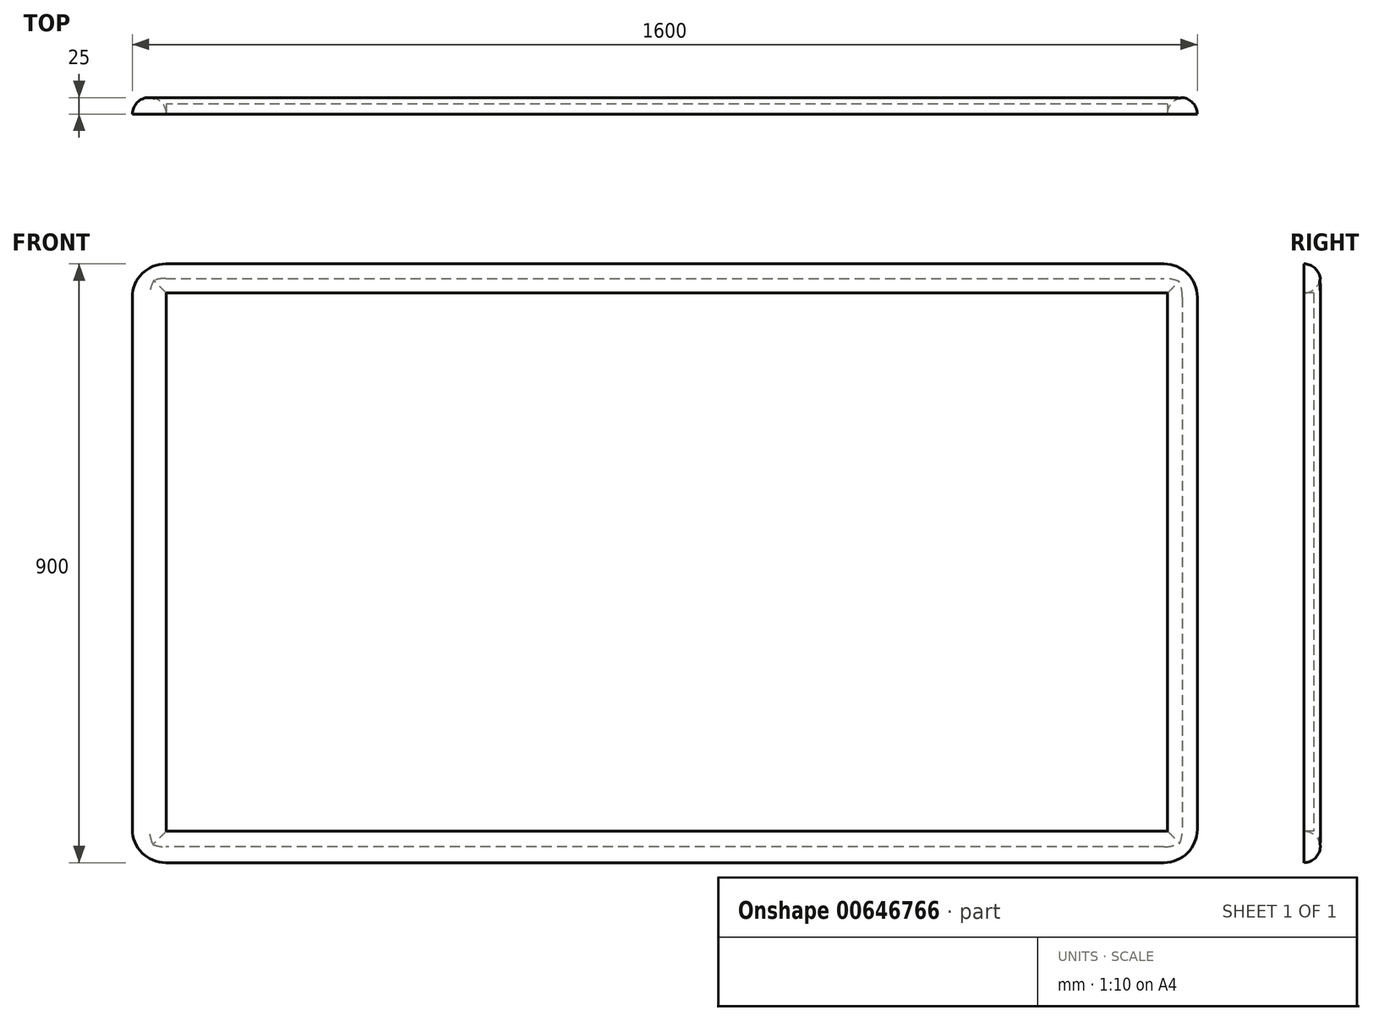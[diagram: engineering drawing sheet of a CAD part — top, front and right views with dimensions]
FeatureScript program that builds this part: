
annotation { "Feature Type Name" : "Feature", "Feature Type Description" : "" }
export const myFeature = defineFeature(function(context is Context, id is Id, definition is map)
    precondition{}
    {
        {
            var Q0;
            Q0=qCreatedBy(makeId("Front.planeOp"),FACE);
            var sketch = newSketch(context, id + "F0", { "sketchPlane" : qUnion([Q0])});
            skLineSegment(sketch, "E0.bottom", {"start": v(801.75, 391.43) * mm, "end": v(-798.25, 391.43) * mm});
            skLineSegment(sketch, "E0.top", {"start": v(801.75, -508.57) * mm, "end": v(-798.25, -508.57) * mm});
            skLineSegment(sketch, "E0.left", {"start": v(801.75, 391.43) * mm, "end": v(801.75, -508.57) * mm});
            skLineSegment(sketch, "E0.right", {"start": v(-798.25, 391.43) * mm, "end": v(-798.25, -508.57) * mm});
            skLineSegment(sketch, "E1.bottom", {"start": v(757.12, 347.64) * mm, "end": v(-747.15, 347.64) * mm});
            skLineSegment(sketch, "E1.top", {"start": v(757.12, -461.1) * mm, "end": v(-747.15, -461.1) * mm});
            skLineSegment(sketch, "E1.left", {"start": v(757.12, 347.64) * mm, "end": v(757.12, -461.1) * mm});
            skLineSegment(sketch, "E1.right", {"start": v(-747.15, 347.64) * mm, "end": v(-747.15, -461.1) * mm});
            skSolve(sketch);
        }
        {
            var Q0;
            Q0=makeQuery(id+"F0.imprint","IMPRINT",FACE,{"disambiguationData":[TD([[makeQuery(id+"F0.imprint","IMPRINT",EDGE,{"derivedFrom":sQuery(id+"F0.wireOp",EDGE,"E0.bottom")}),1.0]])]});
            extrude(context, id + "F1", {"entities" : qUnion([Q0]), "depth" : 25 * mm, "offsetDistance" : 25 * mm});
        }
        {
            var Q0;
            Q0=makeQuery(id+"F1.opExtrude","CAP_FACE",FACE,{"disambiguationData":[OSD([sQuery(id+"F0.wireOp",EDGE,"E0.bottom"),sQuery(id+"F0.wireOp",EDGE,"E0.top"),sQuery(id+"F0.wireOp",EDGE,"E0.left"),sQuery(id+"F0.wireOp",EDGE,"E0.right"),sQuery(id+"F0.wireOp",EDGE,"E1.bottom"),sQuery(id+"F0.wireOp",EDGE,"E1.top"),sQuery(id+"F0.wireOp",EDGE,"E1.left"),sQuery(id+"F0.wireOp",EDGE,"E1.right")])],"isStart":false});
            var sketch = newSketch(context, id + "F2", { "sketchPlane" : qUnion([Q0])});
            skLineSegment(sketch, "E2.bottom", {"start": v(757.12, 347.64) * mm, "end": v(-747.15, 347.64) * mm});
            skLineSegment(sketch, "E2.top", {"start": v(757.12, -461.1) * mm, "end": v(-747.15, -461.1) * mm});
            skLineSegment(sketch, "E2.left", {"start": v(757.12, 347.64) * mm, "end": v(757.12, -461.1) * mm});
            skLineSegment(sketch, "E2.right", {"start": v(-747.15, 347.64) * mm, "end": v(-747.15, -461.1) * mm});
            skSolve(sketch);
        }
        {
            var Q0;
            Q0 = qSketchRegion(id + "F2", true);
            extrude(context, id + "F3", {"entities" : qUnion([Q0]), "oppositeDirection" : true, "depth" : 15 * mm, "offsetDistance" : 25 * mm});
        }
        {
            var Q0;
            Q0=makeQuery(id+"F1.opExtrude","SWEPT_EDGE",EDGE,{"disambiguationData":[OSD([sQuery(id+"F0.wireOp",EDGE,"E0.bottom"),sQuery(id+"F0.wireOp",EDGE,"E0.left")])]});
            var Q1;
            Q1=makeQuery(id+"F1.opExtrude","SWEPT_EDGE",EDGE,{"disambiguationData":[OSD([sQuery(id+"F0.wireOp",EDGE,"E0.top"),sQuery(id+"F0.wireOp",EDGE,"E0.left")])]});
            var Q2;
            Q2=makeQuery(id+"F1.opExtrude","SWEPT_EDGE",EDGE,{"disambiguationData":[OSD([sQuery(id+"F0.wireOp",EDGE,"E0.top"),sQuery(id+"F0.wireOp",EDGE,"E0.right")])]});
            var Q3;
            Q3=makeQuery(id+"F1.opExtrude","SWEPT_EDGE",EDGE,{"disambiguationData":[OSD([sQuery(id+"F0.wireOp",EDGE,"E0.bottom"),sQuery(id+"F0.wireOp",EDGE,"E0.right")])]});
            fillet(context, id + "F4", {"entities" : qUnion([Q0, Q1, Q2, Q3]), "radius" : 50 * mm, "tangentPropagation" : true, "allowEdgeOverflow" : false});
        }
        {
            var Q0;
            Q0=makeQuery(id+"F1.opExtrude","CAP_EDGE",EDGE,{"disambiguationData":[OSD([sQuery(id+"F0.wireOp",EDGE,"E1.left")])],"isStart":true});
            var Q1;
            Q1=makeQuery(id+"F1.opExtrude","CAP_EDGE",EDGE,{"disambiguationData":[OSD([sQuery(id+"F0.wireOp",EDGE,"E1.bottom")])],"isStart":true});
            var Q2;
            Q2=makeQuery(id+"F1.opExtrude","CAP_EDGE",EDGE,{"disambiguationData":[OSD([sQuery(id+"F0.wireOp",EDGE,"E1.top")])],"isStart":true});
            var Q3;
            Q3=makeQuery(id+"F1.opExtrude","CAP_EDGE",EDGE,{"disambiguationData":[OSD([sQuery(id+"F0.wireOp",EDGE,"E1.right")])],"isStart":true});
            var Q4;
            Q4=makeQuery(id+"F1.opExtrude","CAP_EDGE",EDGE,{"disambiguationData":[OSD([sQuery(id+"F0.wireOp",EDGE,"E0.right")])],"isStart":true});
            var Q5;
            {var subQ0=sQuery(id+"F0.wireOp",EDGE,"E0.right");var subQ1=sQuery(id+"F0.wireOp",EDGE,"E0.bottom");Q5=makeQuery(id+"F4.opFillet","BLEND_EDGE",EDGE,{"blendedFrom":[makeQuery(id+"F1.opExtrude","SWEPT_EDGE",EDGE,{"disambiguationData":[OSD([subQ1,subQ0])]}),makeQuery(id+"F1.opExtrude","CAP_FACE",FACE,{"disambiguationData":[OSD([subQ1,sQuery(id+"F0.wireOp",EDGE,"E0.top"),sQuery(id+"F0.wireOp",EDGE,"E0.left"),subQ0,sQuery(id+"F0.wireOp",EDGE,"E1.bottom"),sQuery(id+"F0.wireOp",EDGE,"E1.top"),sQuery(id+"F0.wireOp",EDGE,"E1.left"),sQuery(id+"F0.wireOp",EDGE,"E1.right")])],"isStart":true})],"blendedInto":[makeQuery(id+"F1.opExtrude","CAP_FACE",FACE,{"disambiguationData":[OSD([subQ1,sQuery(id+"F0.wireOp",EDGE,"E0.top"),sQuery(id+"F0.wireOp",EDGE,"E0.left"),subQ0,sQuery(id+"F0.wireOp",EDGE,"E1.bottom"),sQuery(id+"F0.wireOp",EDGE,"E1.top"),sQuery(id+"F0.wireOp",EDGE,"E1.left"),sQuery(id+"F0.wireOp",EDGE,"E1.right")])],"isStart":true})]});}
            var Q6;
            Q6=makeQuery(id+"F1.opExtrude","CAP_EDGE",EDGE,{"disambiguationData":[OSD([sQuery(id+"F0.wireOp",EDGE,"E0.bottom")])],"isStart":true});
            var Q7;
            {var subQ0=sQuery(id+"F0.wireOp",EDGE,"E0.left");var subQ1=sQuery(id+"F0.wireOp",EDGE,"E0.bottom");Q7=makeQuery(id+"F4.opFillet","BLEND_EDGE",EDGE,{"blendedFrom":[makeQuery(id+"F1.opExtrude","SWEPT_EDGE",EDGE,{"disambiguationData":[OSD([subQ1,subQ0])]}),makeQuery(id+"F1.opExtrude","CAP_FACE",FACE,{"disambiguationData":[OSD([subQ1,sQuery(id+"F0.wireOp",EDGE,"E0.top"),subQ0,sQuery(id+"F0.wireOp",EDGE,"E0.right"),sQuery(id+"F0.wireOp",EDGE,"E1.bottom"),sQuery(id+"F0.wireOp",EDGE,"E1.top"),sQuery(id+"F0.wireOp",EDGE,"E1.left"),sQuery(id+"F0.wireOp",EDGE,"E1.right")])],"isStart":true})],"blendedInto":[makeQuery(id+"F1.opExtrude","CAP_FACE",FACE,{"disambiguationData":[OSD([subQ1,sQuery(id+"F0.wireOp",EDGE,"E0.top"),subQ0,sQuery(id+"F0.wireOp",EDGE,"E0.right"),sQuery(id+"F0.wireOp",EDGE,"E1.bottom"),sQuery(id+"F0.wireOp",EDGE,"E1.top"),sQuery(id+"F0.wireOp",EDGE,"E1.left"),sQuery(id+"F0.wireOp",EDGE,"E1.right")])],"isStart":true})]});}
            var Q8;
            Q8=makeQuery(id+"F1.opExtrude","CAP_EDGE",EDGE,{"disambiguationData":[OSD([sQuery(id+"F0.wireOp",EDGE,"E0.left")])],"isStart":true});
            var Q9;
            {var subQ0=sQuery(id+"F0.wireOp",EDGE,"E0.left");var subQ1=sQuery(id+"F0.wireOp",EDGE,"E0.top");Q9=makeQuery(id+"F4.opFillet","BLEND_EDGE",EDGE,{"blendedFrom":[makeQuery(id+"F1.opExtrude","SWEPT_EDGE",EDGE,{"disambiguationData":[OSD([subQ1,subQ0])]}),makeQuery(id+"F1.opExtrude","CAP_FACE",FACE,{"disambiguationData":[OSD([sQuery(id+"F0.wireOp",EDGE,"E0.bottom"),subQ1,subQ0,sQuery(id+"F0.wireOp",EDGE,"E0.right"),sQuery(id+"F0.wireOp",EDGE,"E1.bottom"),sQuery(id+"F0.wireOp",EDGE,"E1.top"),sQuery(id+"F0.wireOp",EDGE,"E1.left"),sQuery(id+"F0.wireOp",EDGE,"E1.right")])],"isStart":true})],"blendedInto":[makeQuery(id+"F1.opExtrude","CAP_FACE",FACE,{"disambiguationData":[OSD([sQuery(id+"F0.wireOp",EDGE,"E0.bottom"),subQ1,subQ0,sQuery(id+"F0.wireOp",EDGE,"E0.right"),sQuery(id+"F0.wireOp",EDGE,"E1.bottom"),sQuery(id+"F0.wireOp",EDGE,"E1.top"),sQuery(id+"F0.wireOp",EDGE,"E1.left"),sQuery(id+"F0.wireOp",EDGE,"E1.right")])],"isStart":true})]});}
            var Q10;
            Q10=makeQuery(id+"F1.opExtrude","CAP_EDGE",EDGE,{"disambiguationData":[OSD([sQuery(id+"F0.wireOp",EDGE,"E0.top")])],"isStart":true});
            var Q11;
            {var subQ0=sQuery(id+"F0.wireOp",EDGE,"E0.right");var subQ1=sQuery(id+"F0.wireOp",EDGE,"E0.top");Q11=makeQuery(id+"F4.opFillet","BLEND_EDGE",EDGE,{"blendedFrom":[makeQuery(id+"F1.opExtrude","SWEPT_EDGE",EDGE,{"disambiguationData":[OSD([subQ1,subQ0])]}),makeQuery(id+"F1.opExtrude","CAP_FACE",FACE,{"disambiguationData":[OSD([sQuery(id+"F0.wireOp",EDGE,"E0.bottom"),subQ1,sQuery(id+"F0.wireOp",EDGE,"E0.left"),subQ0,sQuery(id+"F0.wireOp",EDGE,"E1.bottom"),sQuery(id+"F0.wireOp",EDGE,"E1.top"),sQuery(id+"F0.wireOp",EDGE,"E1.left"),sQuery(id+"F0.wireOp",EDGE,"E1.right")])],"isStart":true})],"blendedInto":[makeQuery(id+"F1.opExtrude","CAP_FACE",FACE,{"disambiguationData":[OSD([sQuery(id+"F0.wireOp",EDGE,"E0.bottom"),subQ1,sQuery(id+"F0.wireOp",EDGE,"E0.left"),subQ0,sQuery(id+"F0.wireOp",EDGE,"E1.bottom"),sQuery(id+"F0.wireOp",EDGE,"E1.top"),sQuery(id+"F0.wireOp",EDGE,"E1.left"),sQuery(id+"F0.wireOp",EDGE,"E1.right")])],"isStart":true})]});}
            fillet(context, id + "F5", {"entities" : qUnion([Q0, Q1, Q2, Q3, Q4, Q5, Q6, Q7, Q8, Q9, Q10, Q11]), "radius" : 25 * mm, "tangentPropagation" : true, "allowEdgeOverflow" : false});
        }
    });
